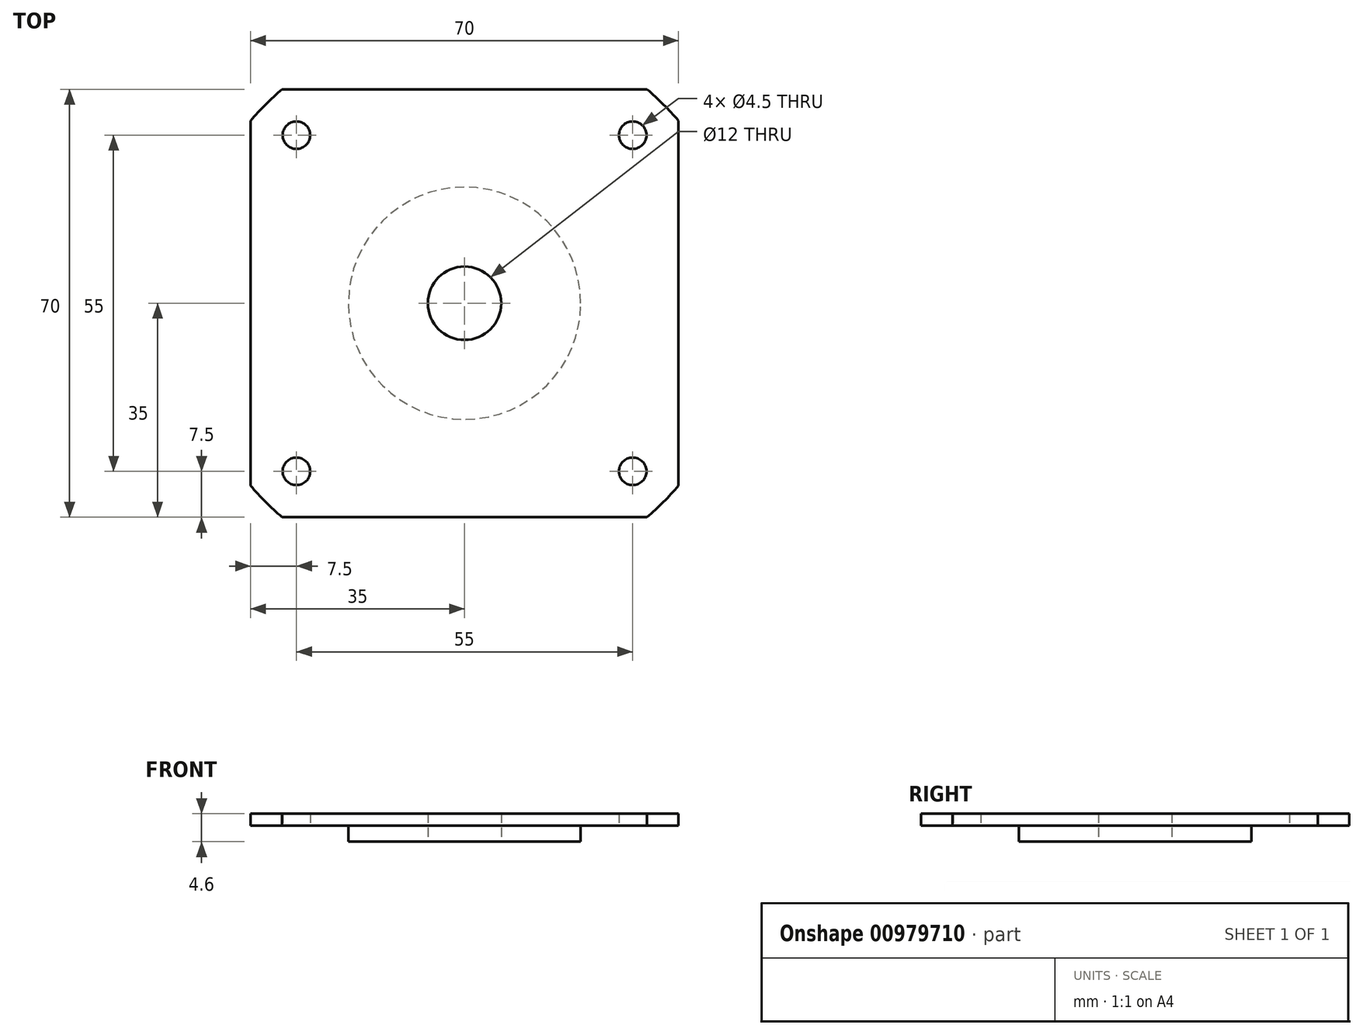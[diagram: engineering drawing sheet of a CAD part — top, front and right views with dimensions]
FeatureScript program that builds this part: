
annotation { "Feature Type Name" : "Feature", "Feature Type Description" : "" }
export const myFeature = defineFeature(function(context is Context, id is Id, definition is map)
    precondition{}
    {
        {
            var Q0;
            Q0=qCreatedBy(makeId("Top.planeOp"),FACE);
            var sketch = newSketch(context, id + "F0", { "sketchPlane" : qUnion([Q0])});
            skArc(sketch, "E0", {"start": v(-29.85, 35) * mm, "mid": v(-32.53, 32.53) * mm, "end": v(-35, 29.85) * mm});
            skLineSegment(sketch, "E1.bottom", {"start": v(-27.5, 27.5) * mm, "end": v(27.5, 27.5) * mm, "construction": true});
            skLineSegment(sketch, "E1.top", {"start": v(-27.5, -27.5) * mm, "end": v(27.5, -27.5) * mm, "construction": true});
            skLineSegment(sketch, "E1.left", {"start": v(-27.5, 27.5) * mm, "end": v(-27.5, -27.5) * mm, "construction": true});
            skLineSegment(sketch, "E1.right", {"start": v(27.5, 27.5) * mm, "end": v(27.5, -27.5) * mm, "construction": true});
            skCircle(sketch, "E2", {"center": v(-27.5, 27.5) * mm, "radius": 2.25 * mm});
            skCircle(sketch, "E3", {"center": v(27.5, 27.5) * mm, "radius": 2.25 * mm});
            skCircle(sketch, "E4", {"center": v(27.5, -27.5) * mm, "radius": 2.25 * mm});
            skCircle(sketch, "E5", {"center": v(-27.5, -27.5) * mm, "radius": 2.25 * mm});
            skCircle(sketch, "E6", {"center": v(0, 0) * mm, "radius": 6 * mm});
            skLineSegment(sketch, "E7.bottom", {"start": v(29.85, 35) * mm, "end": v(-29.85, 35) * mm});
            skLineSegment(sketch, "E7.top", {"start": v(29.85, -35) * mm, "end": v(-29.85, -35) * mm});
            skLineSegment(sketch, "E7.left", {"start": v(35, 29.85) * mm, "end": v(35, -29.85) * mm});
            skLineSegment(sketch, "E7.right", {"start": v(-35, 29.85) * mm, "end": v(-35, -29.85) * mm});
            skPoint(sketch, "E8.orphan", {"position": v(-35, 35) * mm});
            skArc(sketch, "E9.trimOffspring", {"start": v(29.85, -35) * mm, "mid": v(32.53, -32.53) * mm, "end": v(35, -29.85) * mm});
            skPoint(sketch, "E10.orphan", {"position": v(-35, -35) * mm});
            skArc(sketch, "E11.trimOffspring", {"start": v(-35, -29.85) * mm, "mid": v(-32.53, -32.53) * mm, "end": v(-29.85, -35) * mm});
            skPoint(sketch, "E12.orphan", {"position": v(35, 35) * mm});
            skPoint(sketch, "E13.orphan", {"position": v(35, -35) * mm});
            skArc(sketch, "E14.trimOffspring", {"start": v(35, 29.85) * mm, "mid": v(32.53, 32.53) * mm, "end": v(29.85, 35) * mm});
            skSolve(sketch);
        }
        {
            var Q0;
            Q0 = qSketchRegion(id + "F0", true);
            extrude(context, id + "F1", {"entities" : qUnion([Q0]), "depth" : 2 * mm, "offsetDistance" : 25 * mm});
        }
        {
            var Q0;
            Q0=makeQuery(id+"F1.opExtrude","CAP_FACE",FACE,{"disambiguationData":[OSD([sQuery(id+"F0.wireOp",EDGE,"E0"),sQuery(id+"F0.wireOp",EDGE,"E2"),sQuery(id+"F0.wireOp",EDGE,"E3"),sQuery(id+"F0.wireOp",EDGE,"E4"),sQuery(id+"F0.wireOp",EDGE,"E5"),sQuery(id+"F0.wireOp",EDGE,"E6"),sQuery(id+"F0.wireOp",EDGE,"E7.bottom"),sQuery(id+"F0.wireOp",EDGE,"E7.top"),sQuery(id+"F0.wireOp",EDGE,"E7.left"),sQuery(id+"F0.wireOp",EDGE,"E7.right"),sQuery(id+"F0.wireOp",EDGE,"E9.trimOffspring"),sQuery(id+"F0.wireOp",EDGE,"E11.trimOffspring"),sQuery(id+"F0.wireOp",EDGE,"E14.trimOffspring")])],"isStart":false});
            var sketch = newSketch(context, id + "F2", { "sketchPlane" : qUnion([Q0])});
            skCircle(sketch, "E15", {"center": v(0, 0) * mm, "radius": 19 * mm});
            skCircle(sketch, "E16", {"center": v(0, 0) * mm, "radius": 6 * mm});
            skSolve(sketch);
        }
        {
            var Q0;
            Q0 = qSketchRegion(id + "F2", true);
            extrude(context, id + "F3", {"entities" : qUnion([Q0]), "operationType" : NewBodyOperationType.ADD, "oppositeDirection" : true, "depth" : 4.6 * mm, "offsetDistance" : 25 * mm});
        }
    });
